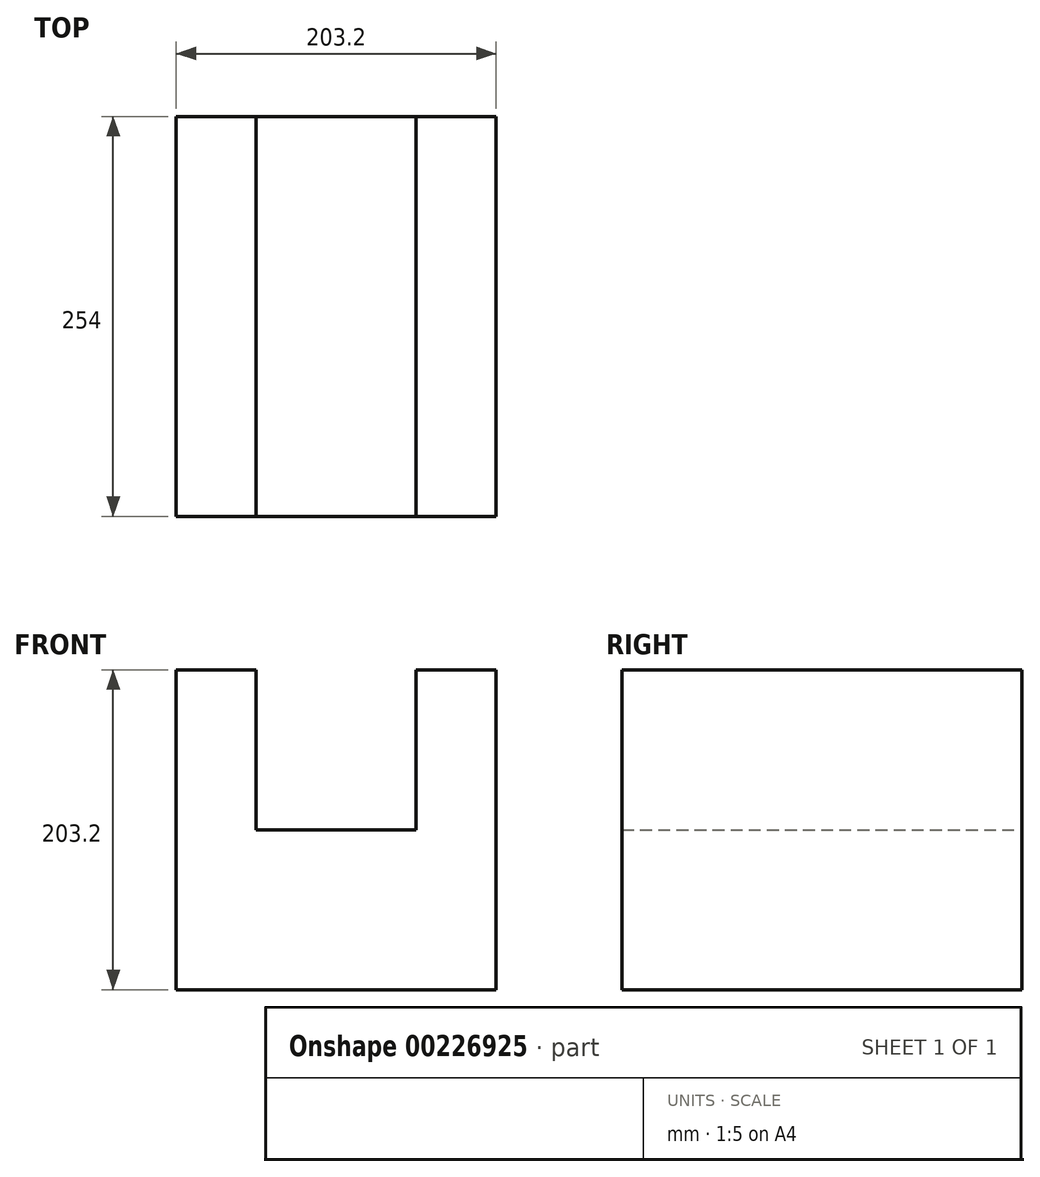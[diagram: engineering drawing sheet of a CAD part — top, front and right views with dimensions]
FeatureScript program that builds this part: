
annotation { "Feature Type Name" : "Feature", "Feature Type Description" : "" }
export const myFeature = defineFeature(function(context is Context, id is Id, definition is map)
    precondition{}
    {
        {
            var Q0;
            Q0=qCreatedBy(makeId("Front.planeOp"),FACE);
            var sketch = newSketch(context, id + "F0", { "sketchPlane" : qUnion([Q0])});
            skLineSegment(sketch, "E0.bottom", {"start": v(-127, 91.97) * mm, "end": v(-76.2, 91.97) * mm});
            skLineSegment(sketch, "E0.top", {"start": v(-127, -111.23) * mm, "end": v(76.2, -111.23) * mm});
            skLineSegment(sketch, "E0.left", {"start": v(-127, 91.97) * mm, "end": v(-127, -111.23) * mm});
            skLineSegment(sketch, "E0.right", {"start": v(76.2, 91.97) * mm, "end": v(76.2, -111.23) * mm});
            skLineSegment(sketch, "E1.top", {"start": v(-76.2, -9.63) * mm, "end": v(25.4, -9.63) * mm});
            skLineSegment(sketch, "E1.left", {"start": v(-76.2, 91.97) * mm, "end": v(-76.2, -9.63) * mm});
            skLineSegment(sketch, "E1.right", {"start": v(25.4, 91.97) * mm, "end": v(25.4, -9.63) * mm});
            skLineSegment(sketch, "E2.trimOffspring", {"start": v(25.4, 91.97) * mm, "end": v(76.2, 91.97) * mm});
            skSolve(sketch);
        }
        {
            var Q0;
            Q0 = qSketchRegion(id + "F0", true);
            extrude(context, id + "F1", {"entities" : qUnion([Q0]), "depth" : 254 * mm});
        }
    });
